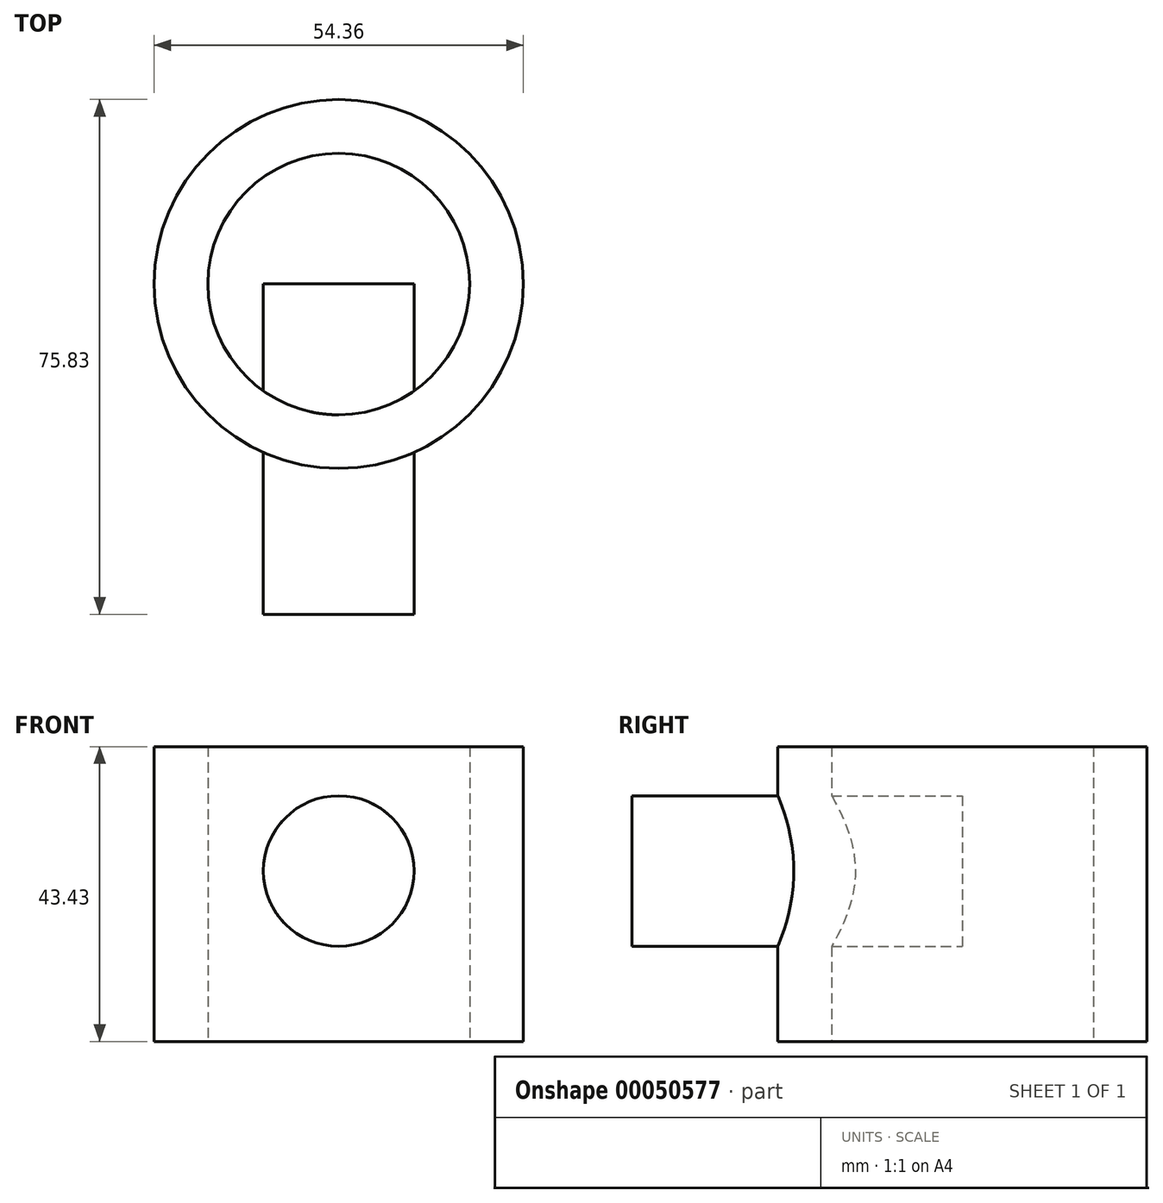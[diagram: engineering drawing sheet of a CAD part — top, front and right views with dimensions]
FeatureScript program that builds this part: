
annotation { "Feature Type Name" : "Feature", "Feature Type Description" : "" }
export const myFeature = defineFeature(function(context is Context, id is Id, definition is map)
    precondition{}
    {
        {
            var Q0;
            Q0=qCreatedBy(makeId("Top.planeOp"),FACE);
            var sketch = newSketch(context, id + "F0", { "sketchPlane" : qUnion([Q0])});
            skCircle(sketch, "E0", {"center": v(0, 0) * mm, "radius": 27.18 * mm});
            skCircle(sketch, "E1", {"center": v(0, 0) * mm, "radius": 19.27 * mm});
            skSolve(sketch);
        }
        {
            var Q0;
            Q0=qSketchRegion(id+"F0",true);
            extrude(context, id + "F1", {"entities" : qUnion([Q0]), "depth" : 43.43 * mm});
        }
        {
            var Q0;
            Q0=qCreatedBy(makeId("Front.planeOp"),FACE);
            var sketch = newSketch(context, id + "F2", { "sketchPlane" : qUnion([Q0])});
            skCircle(sketch, "E2", {"center": v(0, 25.1) * mm, "radius": 11.1 * mm});
            skSolve(sketch);
        }
        {
            var Q0;
            Q0=makeQuery(id+"F2.imprint","IMPRINT",FACE,{"disambiguationData":[TD([[makeQuery(id+"F2.imprint","IMPRINT",EDGE,{"derivedFrom":sQuery(id+"F2.wireOp",EDGE,"E2")}),1.0]])]});
            extrude(context, id + "F3", {"entities" : qUnion([Q0]), "operationType" : NewBodyOperationType.ADD, "depth" : 48.65 * mm});
        }
    });
